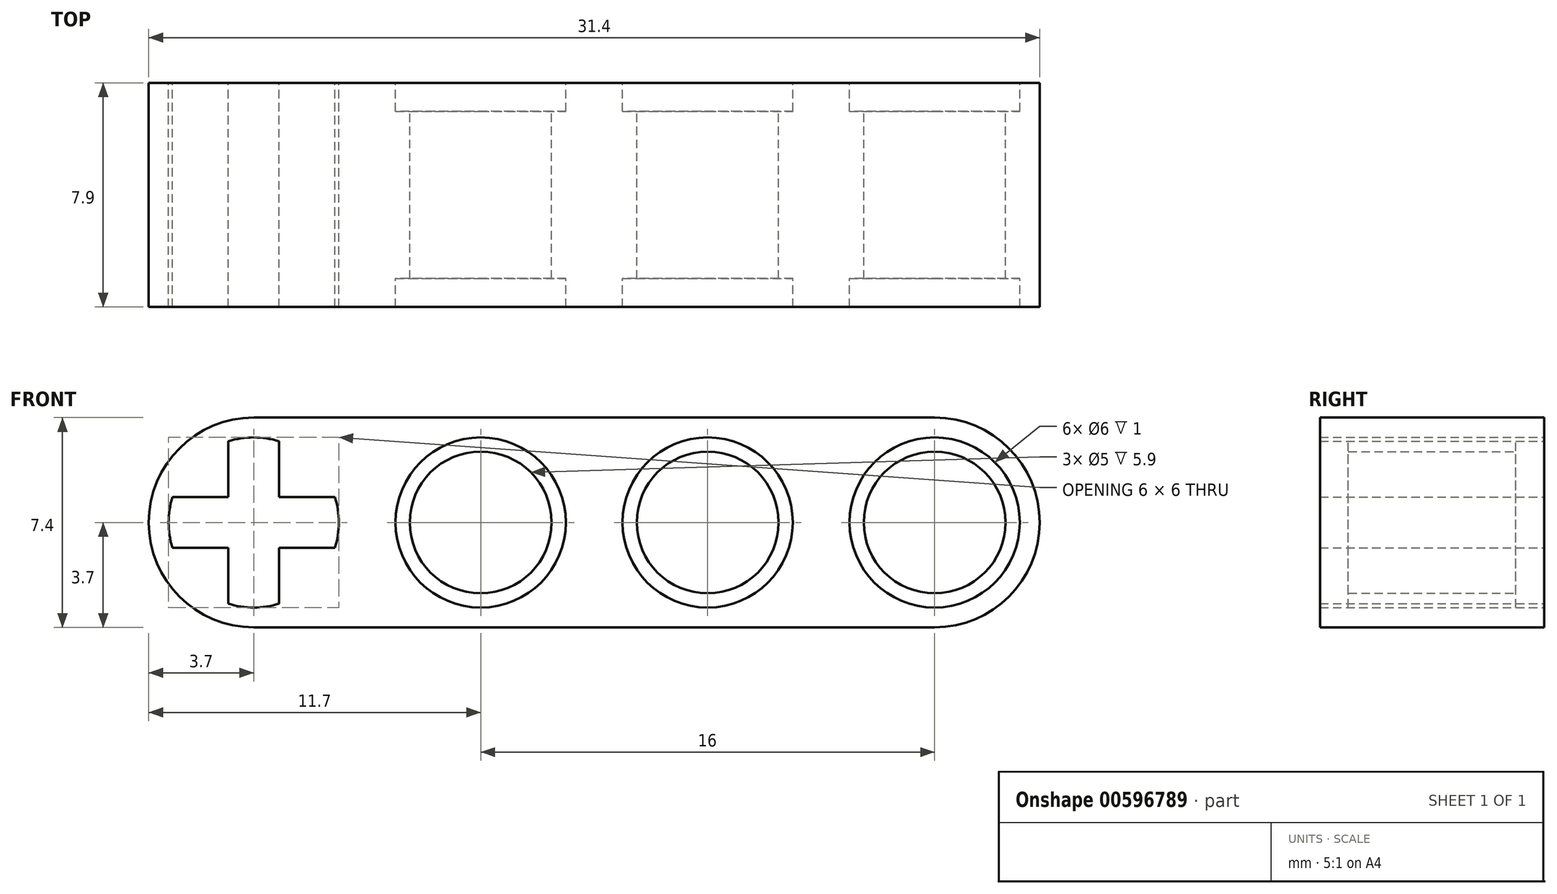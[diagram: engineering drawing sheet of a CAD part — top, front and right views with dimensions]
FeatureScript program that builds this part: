
annotation { "Feature Type Name" : "Feature", "Feature Type Description" : "" }
export const myFeature = defineFeature(function(context is Context, id is Id, definition is map)
    precondition{}
    {
        {
            var Q0;
            Q0=qCreatedBy(makeId("Front.planeOp"),FACE);
            var sketch = newSketch(context, id + "F0", { "sketchPlane" : qUnion([Q0])});
            skLineSegment(sketch, "E0.bottom", {"start": v(15.7, 3.7) * mm, "end": v(-15.7, 3.7) * mm});
            skLineSegment(sketch, "E0.top", {"start": v(15.7, -3.7) * mm, "end": v(-15.7, -3.7) * mm});
            skLineSegment(sketch, "E0.left", {"start": v(15.7, 3.7) * mm, "end": v(15.7, -3.7) * mm});
            skLineSegment(sketch, "E0.right", {"start": v(-15.7, 3.7) * mm, "end": v(-15.7, -3.7) * mm});
            skPoint(sketch, "E0.middle", {"position": v(0, 0) * mm});
            skCircle(sketch, "E1", {"center": v(-4, 0) * mm, "radius": 3 * mm});
            skArc(sketch, "E2", {"start": v(-11.1, 2.86) * mm, "mid": v(-12, 3) * mm, "end": v(-12.9, 2.86) * mm});
            skCircle(sketch, "E3", {"center": v(4, 0) * mm, "radius": 3 * mm});
            skCircle(sketch, "E4", {"center": v(12, 0) * mm, "radius": 3 * mm});
            skLineSegment(sketch, "E5.left", {"start": v(-11.1, 2.86) * mm, "end": v(-11.1, 0.9) * mm});
            skLineSegment(sketch, "E5.right", {"start": v(-12.9, 2.86) * mm, "end": v(-12.9, 0.9) * mm});
            skLineSegment(sketch, "E6.bottom", {"start": v(-9.14, 0.9) * mm, "end": v(-11.1, 0.9) * mm});
            skLineSegment(sketch, "E6.top", {"start": v(-9.14, -0.9) * mm, "end": v(-11.1, -0.9) * mm});
            skPoint(sketch, "E6.left.end.orphan", {"position": v(-8.2, -0.9) * mm});
            skPoint(sketch, "E6.left.start.orphan", {"position": v(-8.2, 0.9) * mm});
            skPoint(sketch, "E7.orphan", {"position": v(-11.1, 3.36) * mm});
            skPoint(sketch, "E8.orphan", {"position": v(-12.9, 3.36) * mm});
            skPoint(sketch, "E5.top.end.orphan", {"position": v(-12.9, -3.36) * mm});
            skPoint(sketch, "E9.orphan", {"position": v(-11.1, -3.36) * mm});
            skLineSegment(sketch, "E10.trimOffspring", {"start": v(-12.9, -0.9) * mm, "end": v(-14.86, -0.9) * mm});
            skLineSegment(sketch, "E11.trimOffspring", {"start": v(-11.1, -0.9) * mm, "end": v(-11.1, -2.86) * mm});
            skLineSegment(sketch, "E12.trimOffspring", {"start": v(-12.9, 0.9) * mm, "end": v(-14.86, 0.9) * mm});
            skLineSegment(sketch, "E13.trimOffspring", {"start": v(-12.9, -0.9) * mm, "end": v(-12.9, -2.86) * mm});
            skPoint(sketch, "E14.trimOffspring.end.orphan", {"position": v(-15.8, -0.9) * mm});
            skPoint(sketch, "E15.trimOffspring.end.orphan", {"position": v(-15.8, 0.9) * mm});
            skArc(sketch, "E16.trimOffspring", {"start": v(-9.14, -0.9) * mm, "mid": v(-9, 0) * mm, "end": v(-9.14, 0.9) * mm});
            skArc(sketch, "E17.trimOffspring", {"start": v(-12.9, -2.86) * mm, "mid": v(-12, -3) * mm, "end": v(-11.1, -2.86) * mm});
            skArc(sketch, "E18.trimOffspring", {"start": v(-14.86, 0.9) * mm, "mid": v(-15, 0) * mm, "end": v(-14.86, -0.9) * mm});
            skCircle(sketch, "E19", {"center": v(-4, 0) * mm, "radius": 2.5 * mm});
            skCircle(sketch, "E20", {"center": v(4, 0) * mm, "radius": 2.5 * mm});
            skCircle(sketch, "E21", {"center": v(12, 0) * mm, "radius": 2.5 * mm});
            skSolve(sketch);
        }
        {
            var Q0;
            Q0=qSketchRegion(id+"F0",true);
            extrude(context, id + "F1", {"entities" : qUnion([Q0]), "endBound" : BoundingType.SYMMETRIC, "depth" : 7.9 * mm, "offsetDistance" : 25 * mm});
        }
        {
            var Q0;
            Q0=makeQuery(id+"F0.imprint","IMPRINT",FACE,{"disambiguationData":[TD([[makeQuery(id+"F0.imprint","IMPRINT",EDGE,{"derivedFrom":sQuery(id+"F0.wireOp",EDGE,"E1")}),1.0]])]});
            var Q1;
            Q1=makeQuery(id+"F0.imprint","IMPRINT",FACE,{"disambiguationData":[TD([[makeQuery(id+"F0.imprint","IMPRINT",EDGE,{"derivedFrom":sQuery(id+"F0.wireOp",EDGE,"E3")}),1.0]])]});
            var Q2;
            Q2=makeQuery(id+"F0.imprint","IMPRINT",FACE,{"disambiguationData":[TD([[makeQuery(id+"F0.imprint","IMPRINT",EDGE,{"derivedFrom":sQuery(id+"F0.wireOp",EDGE,"E4")}),1.0]])]});
            extrude(context, id + "F2", {"entities" : qUnion([Q0, Q1, Q2]), "operationType" : NewBodyOperationType.ADD, "endBound" : BoundingType.SYMMETRIC, "depth" : 5.9 * mm, "offsetDistance" : 25 * mm});
        }
        {
            var Q0;
            Q0=makeQuery(id+"F1.opExtrude","SWEPT_EDGE",EDGE,{"disambiguationData":[OSD([sQuery(id+"F0.wireOp",EDGE,"E0.bottom"),sQuery(id+"F0.wireOp",EDGE,"E0.right")])]});
            var Q1;
            Q1=makeQuery(id+"F1.opExtrude","SWEPT_EDGE",EDGE,{"disambiguationData":[OSD([sQuery(id+"F0.wireOp",EDGE,"E0.top"),sQuery(id+"F0.wireOp",EDGE,"E0.right")])]});
            var Q2;
            Q2=makeQuery(id+"F1.opExtrude","SWEPT_EDGE",EDGE,{"disambiguationData":[OSD([sQuery(id+"F0.wireOp",EDGE,"E0.bottom"),sQuery(id+"F0.wireOp",EDGE,"E0.left")])]});
            var Q3;
            Q3=makeQuery(id+"F1.opExtrude","SWEPT_EDGE",EDGE,{"disambiguationData":[OSD([sQuery(id+"F0.wireOp",EDGE,"E0.top"),sQuery(id+"F0.wireOp",EDGE,"E0.left")])]});
            fillet(context, id + "F3", {"entities" : qUnion([Q0, Q1, Q2, Q3]), "radius" : 3.7 * mm, "tangentPropagation" : true, "allowEdgeOverflow" : false});
        }
    });
